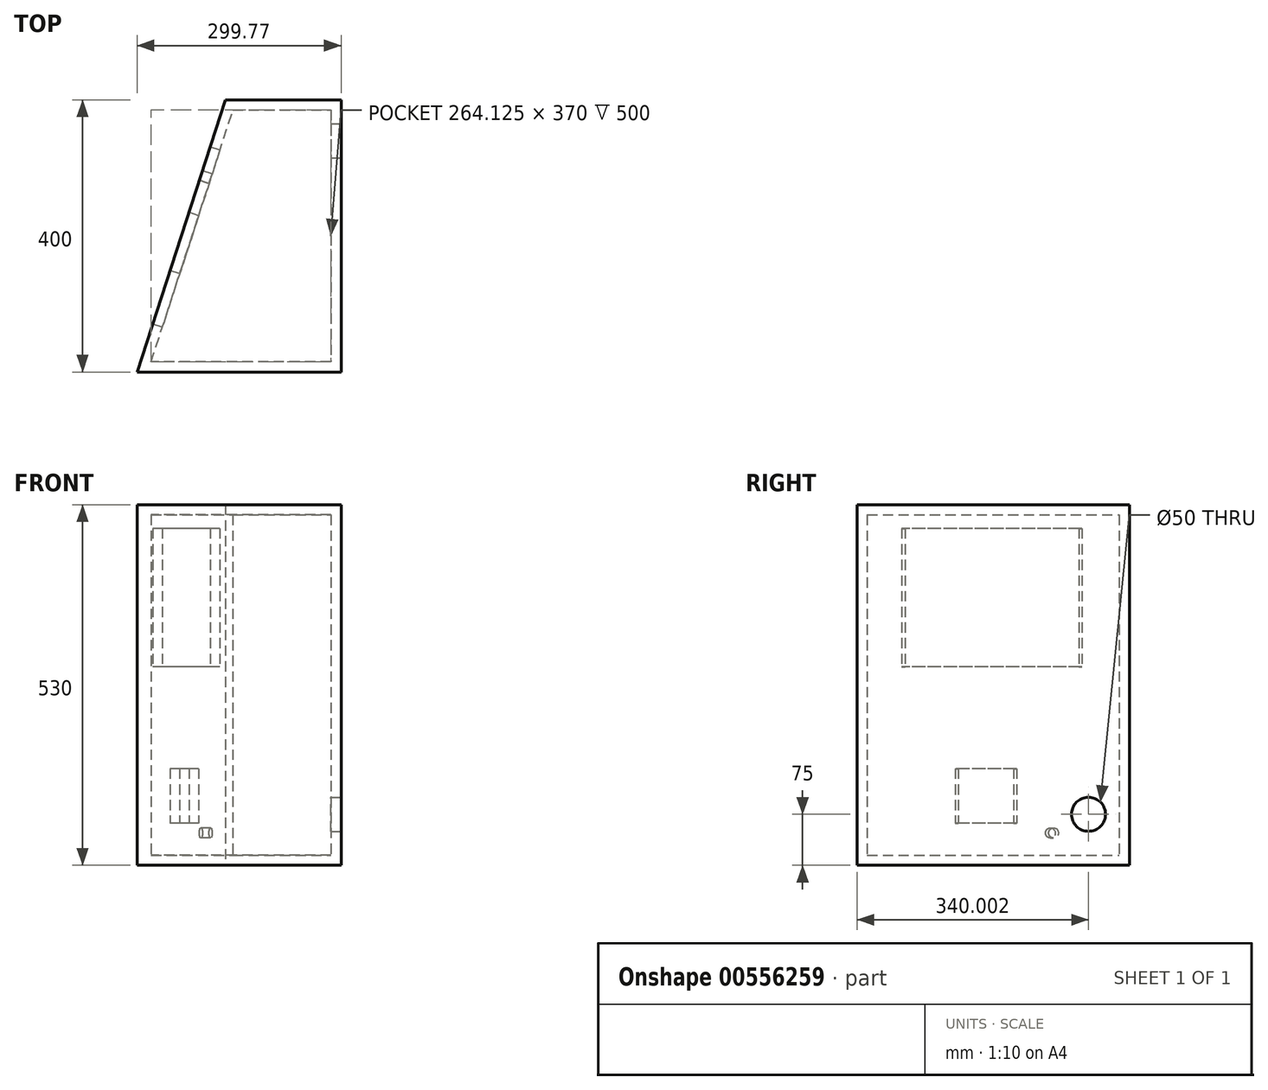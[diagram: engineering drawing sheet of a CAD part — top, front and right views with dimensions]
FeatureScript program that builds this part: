
annotation { "Feature Type Name" : "Feature", "Feature Type Description" : "" }
export const myFeature = defineFeature(function(context is Context, id is Id, definition is map)
    precondition{}
    {
        {
            var Q0;
            Q0=qCreatedBy(makeId("Top.planeOp"),FACE);
            var sketch = newSketch(context, id + "F0", { "sketchPlane" : qUnion([Q0])});
            skLineSegment(sketch, "E0", {"start": v(-46.7, 227.97) * mm, "end": v(123.07, 227.97) * mm});
            skLineSegment(sketch, "E1", {"start": v(123.07, 227.97) * mm, "end": v(123.07, -172.03) * mm});
            skLineSegment(sketch, "E2", {"start": v(123.07, -172.03) * mm, "end": v(-176.7, -172.03) * mm});
            skLineSegment(sketch, "E3", {"start": v(-176.7, -172.03) * mm, "end": v(-46.7, 227.97) * mm});
            skLineSegment(sketch, "E4.0", {"start": v(108.07, 212.97) * mm, "end": v(108.07, -157.03) * mm});
            skLineSegment(sketch, "E4.1", {"start": v(-35.8, 212.97) * mm, "end": v(108.07, 212.97) * mm});
            skLineSegment(sketch, "E4.2", {"start": v(-160.93, -172.03) * mm, "end": v(-30.93, 227.97) * mm});
            skLineSegment(sketch, "E4.3", {"start": v(108.07, -157.03) * mm, "end": v(-156.05, -157.03) * mm});
            skLineSegment(sketch, "E5", {"start": v(-69.26, 158.55) * mm, "end": v(38.2, 123.62) * mm, "construction": true});
            skLineSegment(sketch, "E6", {"start": v(38.2, 123.62) * mm, "end": v(-46.36, -136.58) * mm, "construction": true});
            skLineSegment(sketch, "E7", {"start": v(-46.36, -136.58) * mm, "end": v(-153.83, -101.65) * mm, "construction": true});
            skSolve(sketch);
        }
        {
            var Q0;
            {var subQ1=sQuery(id+"F0.wireOp",EDGE,"E1");Q0=makeQuery(id+"F0.imprint","IMPRINT",FACE,{"disambiguationData":[TD([[makeQuery(id+"F0.imprint","IMPRINT",EDGE,{"derivedFrom":subQ1}),-1.0]])]});}
            var Q1;
            {var subQ4=sQuery(id+"F0.wireOp",EDGE,"E3");Q1=makeQuery(id+"F0.imprint","IMPRINT",FACE,{"disambiguationData":[TD([[makeQuery(id+"F0.imprint","IMPRINT",EDGE,{"derivedFrom":subQ4}),-1.0]])]});}
            extrude(context, id + "F1", {"entities" : qUnion([Q0, Q1]), "depth" : 500 * mm, "offsetDistance" : 25 * mm});
        }
        {
            var Q0;
            Q0=makeQuery(id+"F1.opExtrude","SWEPT_FACE",FACE,{"disambiguationData":[OSD([sQuery(id+"F0.wireOp",EDGE,"E3")])]});
            var sketch = newSketch(context, id + "F2", { "sketchPlane" : qUnion([Q0])});
            skLineSegment(sketch, "E8.bottom", {"start": v(-129.38, 480) * mm, "end": v(144.22, 480) * mm});
            skLineSegment(sketch, "E8.top", {"start": v(-129.38, 277) * mm, "end": v(144.22, 277) * mm});
            skLineSegment(sketch, "E8.left", {"start": v(-129.38, 480) * mm, "end": v(-129.38, 277) * mm});
            skLineSegment(sketch, "E8.right", {"start": v(144.22, 480) * mm, "end": v(144.22, 277) * mm});
            skLineSegment(sketch, "E9.bottom", {"start": v(-28.38, 127) * mm, "end": v(61.62, 127) * mm});
            skLineSegment(sketch, "E9.top", {"start": v(-28.38, 47) * mm, "end": v(61.62, 47) * mm});
            skLineSegment(sketch, "E9.left", {"start": v(-28.38, 127) * mm, "end": v(-28.38, 47) * mm});
            skLineSegment(sketch, "E9.right", {"start": v(61.62, 127) * mm, "end": v(61.62, 47) * mm});
            skCircle(sketch, "E10", {"center": v(-85.38, 32.5) * mm, "radius": 7.5 * mm});
            skSolve(sketch);
        }
        {
            var Q0;
            Q0=makeQuery(id+"F2.imprint","IMPRINT",FACE,{"disambiguationData":[TD([[makeQuery(id+"F2.imprint","IMPRINT",EDGE,{"derivedFrom":sQuery(id+"F2.wireOp",EDGE,"E8.bottom")}),-1.0]])]});
            var Q1;
            Q1=makeQuery(id+"F2.imprint","IMPRINT",FACE,{"disambiguationData":[TD([[makeQuery(id+"F2.imprint","IMPRINT",EDGE,{"derivedFrom":sQuery(id+"F2.wireOp",EDGE,"E9.bottom")}),-1.0]])]});
            extrude(context, id + "F3", {"entities" : qUnion([Q0, Q1]), "operationType" : NewBodyOperationType.REMOVE, "oppositeDirection" : true, "depth" : 25 * mm, "offsetDistance" : 25 * mm});
        }
        {
            var Q0;
            Q0=makeQuery(id+"F2.imprint","IMPRINT",FACE,{"disambiguationData":[TD([[makeQuery(id+"F2.imprint","IMPRINT",EDGE,{"derivedFrom":sQuery(id+"F2.wireOp",EDGE,"E10")}),1.0]])]});
            extrude(context, id + "F4", {"entities" : qUnion([Q0]), "operationType" : NewBodyOperationType.REMOVE, "oppositeDirection" : true, "depth" : 25 * mm, "offsetDistance" : 25 * mm});
        }
        {
            var Q0;
            Q0=makeQuery(id+"F1.opExtrude","SWEPT_FACE",FACE,{"disambiguationData":[OSD([sQuery(id+"F0.wireOp",EDGE,"E1")])]});
            var sketch = newSketch(context, id + "F5", { "sketchPlane" : qUnion([Q0])});
            skCircle(sketch, "E11", {"center": v(167.97, 60) * mm, "radius": 25 * mm});
            skSolve(sketch);
        }
        {
            var Q0;
            Q0=makeQuery(id+"F5.imprint","IMPRINT",FACE,{"disambiguationData":[TD([[makeQuery(id+"F5.imprint","IMPRINT",EDGE,{"derivedFrom":sQuery(id+"F5.wireOp",EDGE,"E11")}),1.0]])]});
            extrude(context, id + "F6", {"entities" : qUnion([Q0]), "operationType" : NewBodyOperationType.REMOVE, "oppositeDirection" : true, "depth" : 25 * mm, "offsetDistance" : 25 * mm});
        }
        {
            var Q0;
            Q0=makeQuery(id+"F1.opExtrude","CAP_FACE",FACE,{"disambiguationData":[OSD([sQuery(id+"F0.wireOp",EDGE,"E0"),sQuery(id+"F0.wireOp",EDGE,"E1"),sQuery(id+"F0.wireOp",EDGE,"E2"),sQuery(id+"F0.wireOp",EDGE,"E3"),sQuery(id+"F0.wireOp",EDGE,"E4.0"),sQuery(id+"F0.wireOp",EDGE,"E4.1"),sQuery(id+"F0.wireOp",EDGE,"E4.2"),sQuery(id+"F0.wireOp",EDGE,"E4.3")])],"isStart":false});
            var sketch = newSketch(context, id + "F7", { "sketchPlane" : qUnion([Q0])});
            skLineSegment(sketch, "E12", {"start": v(123.07, 227.97) * mm, "end": v(123.07, -172.03) * mm});
            skLineSegment(sketch, "E13", {"start": v(123.07, -172.03) * mm, "end": v(-176.7, -172.03) * mm});
            skLineSegment(sketch, "E14", {"start": v(-176.7, -172.03) * mm, "end": v(-46.7, 227.97) * mm});
            skLineSegment(sketch, "E15", {"start": v(-46.7, 227.97) * mm, "end": v(123.07, 227.97) * mm});
            skSolve(sketch);
        }
        {
            var Q0;
            Q0 = qSketchRegion(id + "F7", true);
            extrude(context, id + "F8", {"entities" : qUnion([Q0]), "operationType" : NewBodyOperationType.ADD, "depth" : 15 * mm, "offsetDistance" : 25 * mm});
        }
        {
            var Q0;
            Q0=makeQuery(id+"F1.opExtrude","CAP_FACE",FACE,{"disambiguationData":[OSD([sQuery(id+"F0.wireOp",EDGE,"E0"),sQuery(id+"F0.wireOp",EDGE,"E1"),sQuery(id+"F0.wireOp",EDGE,"E2"),sQuery(id+"F0.wireOp",EDGE,"E3"),sQuery(id+"F0.wireOp",EDGE,"E4.0"),sQuery(id+"F0.wireOp",EDGE,"E4.1"),sQuery(id+"F0.wireOp",EDGE,"E4.2"),sQuery(id+"F0.wireOp",EDGE,"E4.3")])],"isStart":true});
            var sketch = newSketch(context, id + "F9", { "sketchPlane" : qUnion([Q0])});
            skLineSegment(sketch, "E16", {"start": v(123.07, -227.97) * mm, "end": v(123.07, 172.03) * mm});
            skLineSegment(sketch, "E17", {"start": v(123.07, 172.03) * mm, "end": v(-176.7, 172.03) * mm});
            skLineSegment(sketch, "E18", {"start": v(-176.7, 172.03) * mm, "end": v(-46.7, -227.97) * mm});
            skLineSegment(sketch, "E19", {"start": v(-46.7, -227.97) * mm, "end": v(123.07, -227.97) * mm});
            skSolve(sketch);
        }
        {
            var Q0;
            Q0 = qSketchRegion(id + "F9", true);
            extrude(context, id + "F10", {"entities" : qUnion([Q0]), "operationType" : NewBodyOperationType.ADD, "depth" : 15 * mm, "offsetDistance" : 25 * mm});
        }
    });
